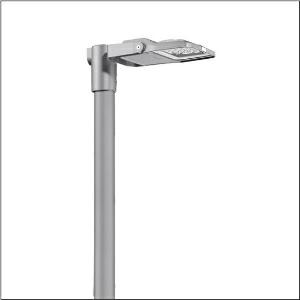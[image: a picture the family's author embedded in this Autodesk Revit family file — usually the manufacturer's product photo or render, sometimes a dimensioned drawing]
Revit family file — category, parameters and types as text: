
# Revit family: floodlight_fl_21_iq_micro___pl52_5xa7762a4d3a_1d61
name_source: partatom
category: Lighting Fixtures
units: mm (PartAtom-declared; Revit-internal decimal feet)

## family parameters
Cut with Voids When Loaded = No
Host = Face
Light Source = No
Part Type = Normal
Room Calculation Point = No
Round Connector Dimension = Use Diameter
Shared = No

## types (1)
- --- (1 x LED, 3010 lm, 23.1 W, 4000K)
    Apparent Load = 23 VA
    CIE Flux Codes = 26 60 98 100 100
    Color Rendering = 70
    Color Temperature = 4000K
    Default Elevation = 1800 mm
    Description = Floodlight FL 21 iQ micro, floodlight, primary light control with lens, of PMMA, primary optical cover: protective disc, of toughened safety glass, transparent, light distribution: PL52, light emission: direct distribution, installation type: surface-mounted, LED, High Power LED, rated luminous flux: 3.010lm, luminous efficacy: 130lm/W, light colour: 740, colour temperature: 4000K, control: Auto-Match, Temp-Guard, Night-Set, Smart-Wire, Desk-Remote (wireless, voltage-free reading and setting of iQ features in the workshop via application-optimized NFC function/RFID function), optimised constant luminous flux control (CLO 2.0), Street-Remote, with terminal, 6-pole, mains connection: 220..240V, AC, 50/60Hz, start of lifetime: 23W, end of service life: 24W, reduction: 11W, luminaire housing, of diecast aluminium, powder-coated, Siteco® metallic grey (DB 702S), corrosivity category C5 mid according to DIN EN ISO 12944, sealing non-destructively replaceable, please order mast flange separately, mast bracket, of steel, galvanised, powder-coated, Siteco® metallic grey (DB 702S), protection rating (complete): IP66, insulation class (complete): insulation class II (safety insulation), certification: CE, ENEC, VDE, protection symbol: D, impact resistance: IK07, permissible operating ambient temperature: -40..+40°C, permissible operating ambient temperature for outdoor applications: -40..+50°C, standard: DIN EN 12944, LABS conformity tested according to VDMA 24364:2018-05, packaging unit: 1 piece

Light Distribution: PL52
    Height = 65 mm
    Lamp = 1 x LED
    Lamp Light Flux = 3010 lm
    Lamp Power = 23.1 W
    Lamp count = 1
    Length = 312 mm
    Luminous efficacy = 130 lm/W
    Manufacturer = Siteco
    ModVariant = No
    Model = 5XA7762A4D3A
    Number of Poles = 1
    OnlyDefault = Yes
    Power Factor = 1
    Product Name = Floodlight FL 21 iQ micro | PL52
    Product group = floodlight | pylon annexe
    ProductGroupID = 6200
    Protection Class = Protection class II
    Protection Degree = IP 66
    RLX_Detail_Level = 1
    RLX_Emergency_Light_Flux = 0 lm
    RLX_Emergency_Type = 0
    RLX_Emergency_Type_DB = No
    RlxData = <blob elided: 101877 chars, md5=5f21e792>
    Socket = socket
    Standby Power = 0 W
    System Light Flux = 3010 lm
    System Power = 23 W
    Type Comments = factory setting: luminous flux: 100 % | dim-lin: 254 | 455 mA
    Type Image = l_1007121.jpg
    URL = http://relux.com
    VarID = @adj_110525
    Voltage = 0 V
    Weight = 0.00 kg
    Width = 230 mm

## geometry (parser evidence)
native form markers: Blend x4, Sweep x13
no freeform markers — native parametric forms only
